# Revit family: Steel-HST Speedbrace-Steel & Tube-Speed Channel
name_source: partatom
category: Structural Framing
revit_build: Autodesk Revit 2018 (Build: 20170927_1515(x64)
units: mm (PartAtom-declared; Revit-internal decimal feet)

## family parameters
Always export as geometry = No
Always vertical = Yes
Cut with Voids When Loaded = No
Material for Model Behavior = Steel
OmniClass Number = 23.25.30.11.14.14
OmniClass Title = Beams
Section Shape = C Profile with Lips
Shared = No
Show family pre-cut in plan views = Yes
Structural Framing Length Roundoff = 0 mm

## types (2) — shared parameters
Assembly Code = B1020370
CBICode = 3411
CBIDescription = Structural steelwork
Centroid Horizontal = 16 mm
Centroid Vertical = 50 mm
Description = The HST Purlins and Girts system utilises speed channel or bolted brace/sag rod components as required by the load tables.
Design Instruction = All the design information should be cross referenced with the current Steel & Tube Purlins and Girts design guide, and AS/NZS 4600:2005
Design Standard = Steel & Tube’s HST purlins and Girts profiles are designed in accordance with AS/NZS 4600:2005.
Height = 100 mm
Inner Fillet = 3 mm
Lip Length = 12.0 mm
Manufacturer = Steel & Tube
ManufacturerName = Steel & Tube
ManufacturerURL = http://www.steelandtube.co.nz
Material Standard = Steel & Tube’s HST purlins and Girts profiles are manufactured from materials conforming to AS1397:2011
ModifiedIssue_ANZRS = 20160526 $
Perimeter = 0.00 m²/m
Principal Axes Angle = 0.00°
SpecificationDescription = Steel & Tube Purlins & Girts
SpecificationReference = 3411ST
Structural Material = Metal-Steel-250MPa
Torsional Modulus = 0.0 mm³
Type Comments = All HST brace channels are manufactured with end-brackets custom fitted to suit the purlin size and spacing.
URL = http://www.steelandtube.co.nz
Uniclass2015Code = Pr_20_76_51_21
Uniclass2015Title = Cold-formed galvanized steel sections
Uniclass2015Version = 2015
Wall Nominal Thickness = 1 mm
Width = 32 mm

## per-type parameters (varying)
| type | Elastic Modulus strong axis | Elastic Modulus weak axis | MassPerUnitLength_ANZRS | Moment of Inertia strong axis | Moment of Inertia weak axis | Nominal Weight | Plastic Modulus strong axis | Plastic Modulus weak axis | Section Area | SectionAreaGross_ANZRS | SectionAreaNet_ANZRS | Shear Area strong axis | Shear Area weak axis | Torsional Moment of Inertia | Wall Design Thickness | Warping Constant |
| 100x32x0.95 | 5030.0 mm³ | 1070.0 mm³ | 1.36 kg/m | 249000.00 mm4 | 23800.00 mm4 | 1.36 kgf/m | 5030.0 mm³ | 1070.0 mm³ | 169.0 mm² | 169.0 mm² | 169.0 mm² | 169.0 mm² | 169.0 mm² | 50.90 mm4 | 0.95 mm | 49900000.0 mm6 |
| 100x32x1.15 | 6040.0 mm³ | 1280.0 mm³ | 1.63 kg/m | 298000.00 mm4 | 28200.00 mm4 | 1.63 kgf/m | 6040.0 mm³ | 1280.0 mm³ | 204.0 mm² | 204.0 mm² | 204.0 mm² | 204.0 mm² | 204.0 mm² | 89.80 mm4 | 1.15 mm | 58800000.0 mm6 |

note: column(s) folded — value = type name in every type: Model

## geometry (parser evidence)
native form markers: Sweep x6
no freeform markers — native parametric forms only
